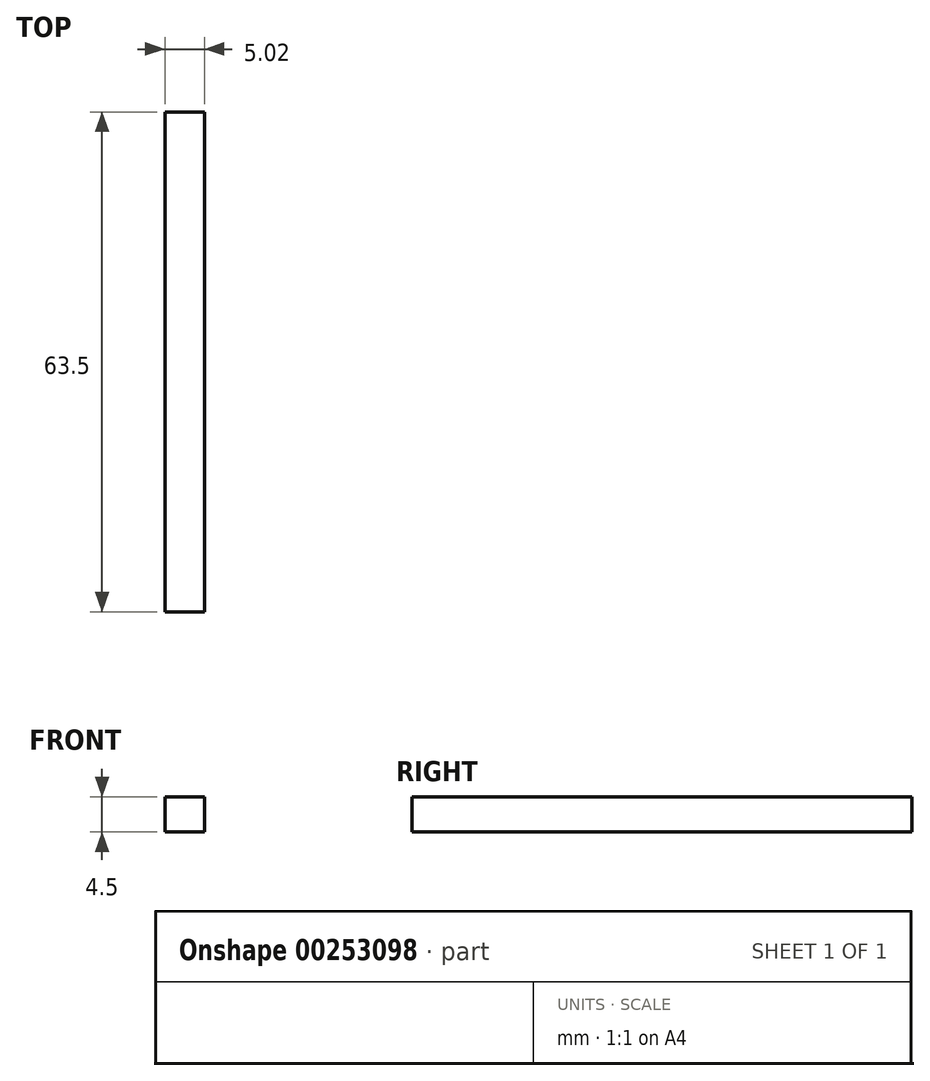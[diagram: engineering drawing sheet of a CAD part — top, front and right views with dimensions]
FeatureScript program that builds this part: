
annotation { "Feature Type Name" : "Feature", "Feature Type Description" : "" }
export const myFeature = defineFeature(function(context is Context, id is Id, definition is map)
    precondition{}
    {
        {
            var Q0;
            Q0=qCreatedBy(makeId("Top.planeOp"),FACE);
            var sketch = newSketch(context, id + "F0", { "sketchPlane" : qUnion([Q0])});
            skLineSegment(sketch, "E0.bottom", {"start": v(-2.5, 63.5) * mm, "end": v(2.5, 63.5) * mm});
            skLineSegment(sketch, "E0.top", {"start": v(-2.5, 0) * mm, "end": v(2.5, 0) * mm});
            skLineSegment(sketch, "E0.left", {"start": v(-2.5, 63.5) * mm, "end": v(-2.5, 0) * mm});
            skLineSegment(sketch, "E0.right", {"start": v(2.5, 63.5) * mm, "end": v(2.5, 0) * mm});
            skSolve(sketch);
        }
        {
            var Q0;
            Q0=makeQuery(id+"F0.imprint","IMPRINT",FACE,{"disambiguationData":[TD([[makeQuery(id+"F0.imprint","IMPRINT",EDGE,{"derivedFrom":sQuery(id+"F0.wireOp",EDGE,"E0.bottom")}),-1.0]])]});
            extrude(context, id + "F1", {"entities" : qUnion([Q0]), "depth" : 4.5 * mm});
        }
    });
